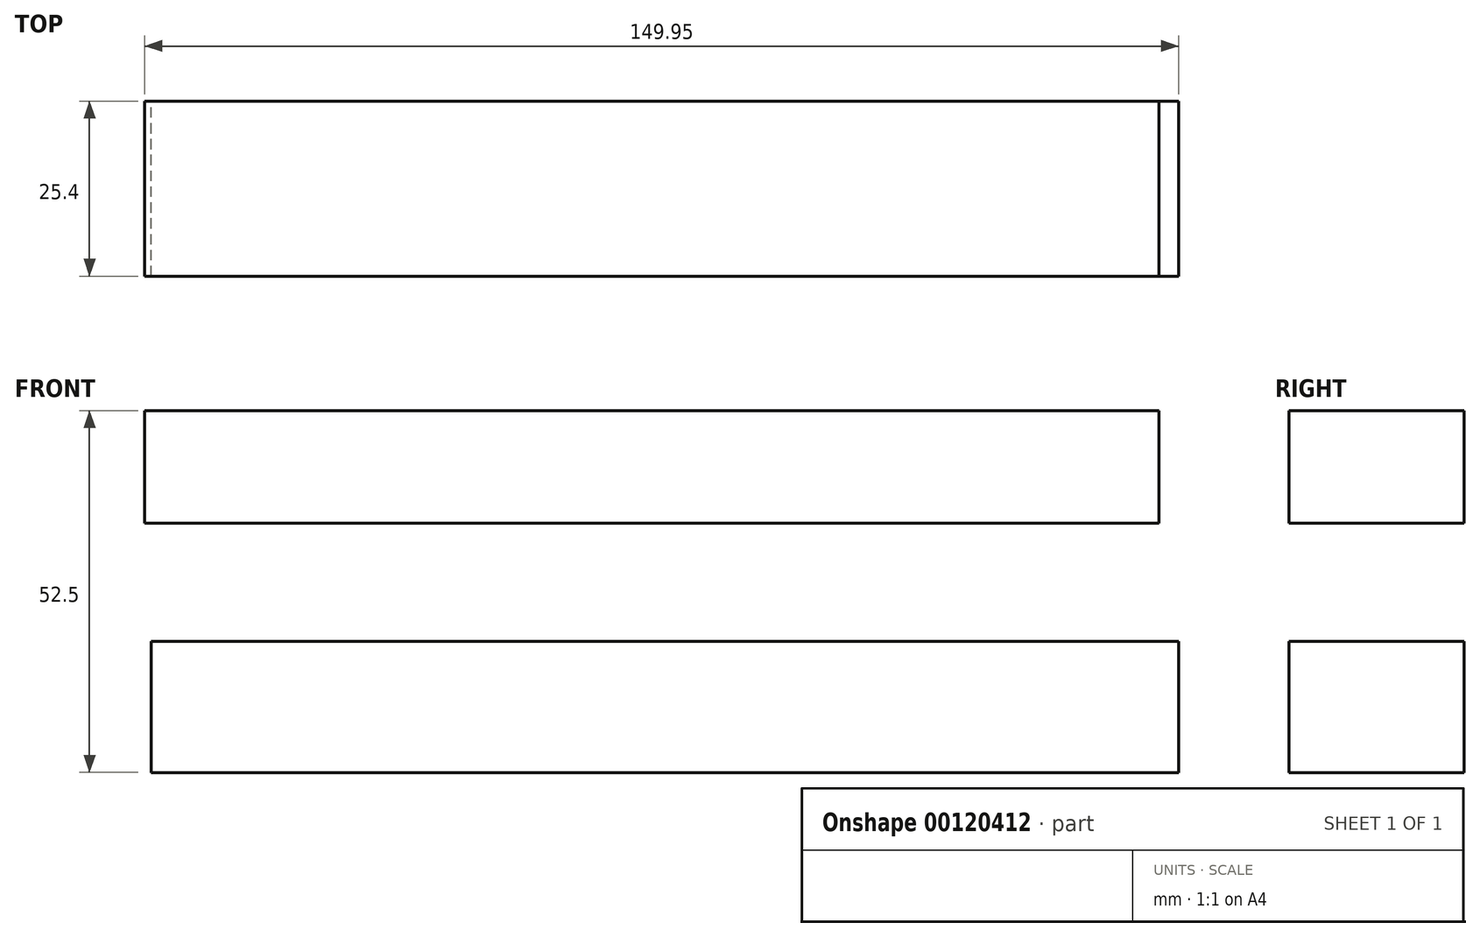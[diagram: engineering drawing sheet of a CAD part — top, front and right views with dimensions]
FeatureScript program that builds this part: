
annotation { "Feature Type Name" : "Feature", "Feature Type Description" : "" }
export const myFeature = defineFeature(function(context is Context, id is Id, definition is map)
    precondition{}
    {
        {
            var Q0;
            Q0=qCreatedBy(makeId("Front.planeOp"),FACE);
            var sketch = newSketch(context, id + "F0", { "sketchPlane" : qUnion([Q0])});
            skLineSegment(sketch, "E0.bottom", {"start": v(-72.46, 17.13) * mm, "end": v(74.67, 17.13) * mm});
            skLineSegment(sketch, "E0.top", {"start": v(-72.46, 33.48) * mm, "end": v(74.67, 33.48) * mm});
            skLineSegment(sketch, "E0.left", {"start": v(-72.46, 17.13) * mm, "end": v(-72.46, 33.48) * mm});
            skLineSegment(sketch, "E0.right", {"start": v(74.67, 17.13) * mm, "end": v(74.67, 33.48) * mm});
            skLineSegment(sketch, "E1.bottom", {"start": v(-47.94, 17.13) * mm, "end": v(-71.52, 17.13) * mm});
            skLineSegment(sketch, "E1.top", {"start": v(-47.94, 0) * mm, "end": v(-71.52, 0) * mm});
            skLineSegment(sketch, "E1.left", {"start": v(-47.94, 17.13) * mm, "end": v(-47.94, 0) * mm});
            skLineSegment(sketch, "E1.right", {"start": v(-71.52, 17.13) * mm, "end": v(-71.52, 0) * mm});
            skLineSegment(sketch, "E2.bottom", {"start": v(-71.52, 0) * mm, "end": v(77.5, 0) * mm});
            skLineSegment(sketch, "E2.top", {"start": v(-71.52, -19.02) * mm, "end": v(77.5, -19.02) * mm});
            skLineSegment(sketch, "E2.left", {"start": v(-71.52, 0) * mm, "end": v(-71.52, -19.02) * mm});
            skLineSegment(sketch, "E2.right", {"start": v(77.5, 0) * mm, "end": v(77.5, -19.02) * mm});
            skLineSegment(sketch, "E3.bottom", {"start": v(16.2, 17.13) * mm, "end": v(43.54, 17.13) * mm});
            skLineSegment(sketch, "E3.top", {"start": v(16.2, 17.13) * mm, "end": v(43.54, 17.13) * mm});
            skLineSegment(sketch, "E3.left", {"start": v(16.2, 17.13) * mm, "end": v(16.2, 17.13) * mm});
            skLineSegment(sketch, "E3.right", {"start": v(43.54, 17.13) * mm, "end": v(43.54, 17.13) * mm});
            skLineSegment(sketch, "E4.bottom", {"start": v(43.54, 17.13) * mm, "end": v(74.67, 17.13) * mm});
            skLineSegment(sketch, "E4.top", {"start": v(43.54, 5.18) * mm, "end": v(74.67, 5.18) * mm});
            skLineSegment(sketch, "E4.left", {"start": v(43.54, 17.13) * mm, "end": v(43.54, 5.18) * mm});
            skLineSegment(sketch, "E4.right", {"start": v(74.67, 17.13) * mm, "end": v(74.67, 5.18) * mm});
            skLineSegment(sketch, "E5.top", {"start": v(16.2, 11.16) * mm, "end": v(43.54, 11.16) * mm});
            skLineSegment(sketch, "E5.left", {"start": v(16.2, 17.13) * mm, "end": v(16.2, 11.16) * mm});
            skLineSegment(sketch, "E5.right", {"start": v(43.54, 17.13) * mm, "end": v(43.54, 11.16) * mm});
            skSolve(sketch);
        }
        {
            var Q0;
            Q0=makeQuery(id+"F0.imprint","IMPRINT",FACE,{"disambiguationData":[TD([[makeQuery(id+"F0.imprint","IMPRINT",EDGE,{"derivedFrom":sQuery(id+"F0.wireOp",EDGE,"E2.top")}),1.0]])]});
            var Q1;
            Q1=makeQuery(id+"F0.imprint","IMPRINT",FACE,{"disambiguationData":[TD([[makeQuery(id+"F0.imprint","IMPRINT",EDGE,{"derivedFrom":sQuery(id+"F0.wireOp",EDGE,"E1.bottom")}),1.0]])]});
            var Q2;
            Q2=makeQuery(id+"F0.imprint","IMPRINT",FACE,{"disambiguationData":[TD([[makeQuery(id+"F0.imprint","IMPRINT",EDGE,{"derivedFrom":sQuery(id+"F0.wireOp",EDGE,"E4.bottom")}),-1.0]])]});
            var Q3;
            Q3=makeQuery(id+"F0.imprint","IMPRINT",FACE,{"disambiguationData":[TD([[makeQuery(id+"F0.imprint","IMPRINT",EDGE,{"derivedFrom":sQuery(id+"F0.wireOp",EDGE,"E3.bottom")}),-1.0]])]});
            var Q4;
            Q4=makeQuery(id+"F0.imprint","IMPRINT",FACE,{"disambiguationData":[TD([[makeQuery(id+"F0.imprint","IMPRINT",EDGE,{"derivedFrom":sQuery(id+"F0.wireOp",EDGE,"E0.top")}),-1.0]])]});
            extrude(context, id + "F1", {"entities" : qUnion([Q0, Q1, Q2, Q3, Q4]), "depth" : 25.4 * mm});
        }
    });
